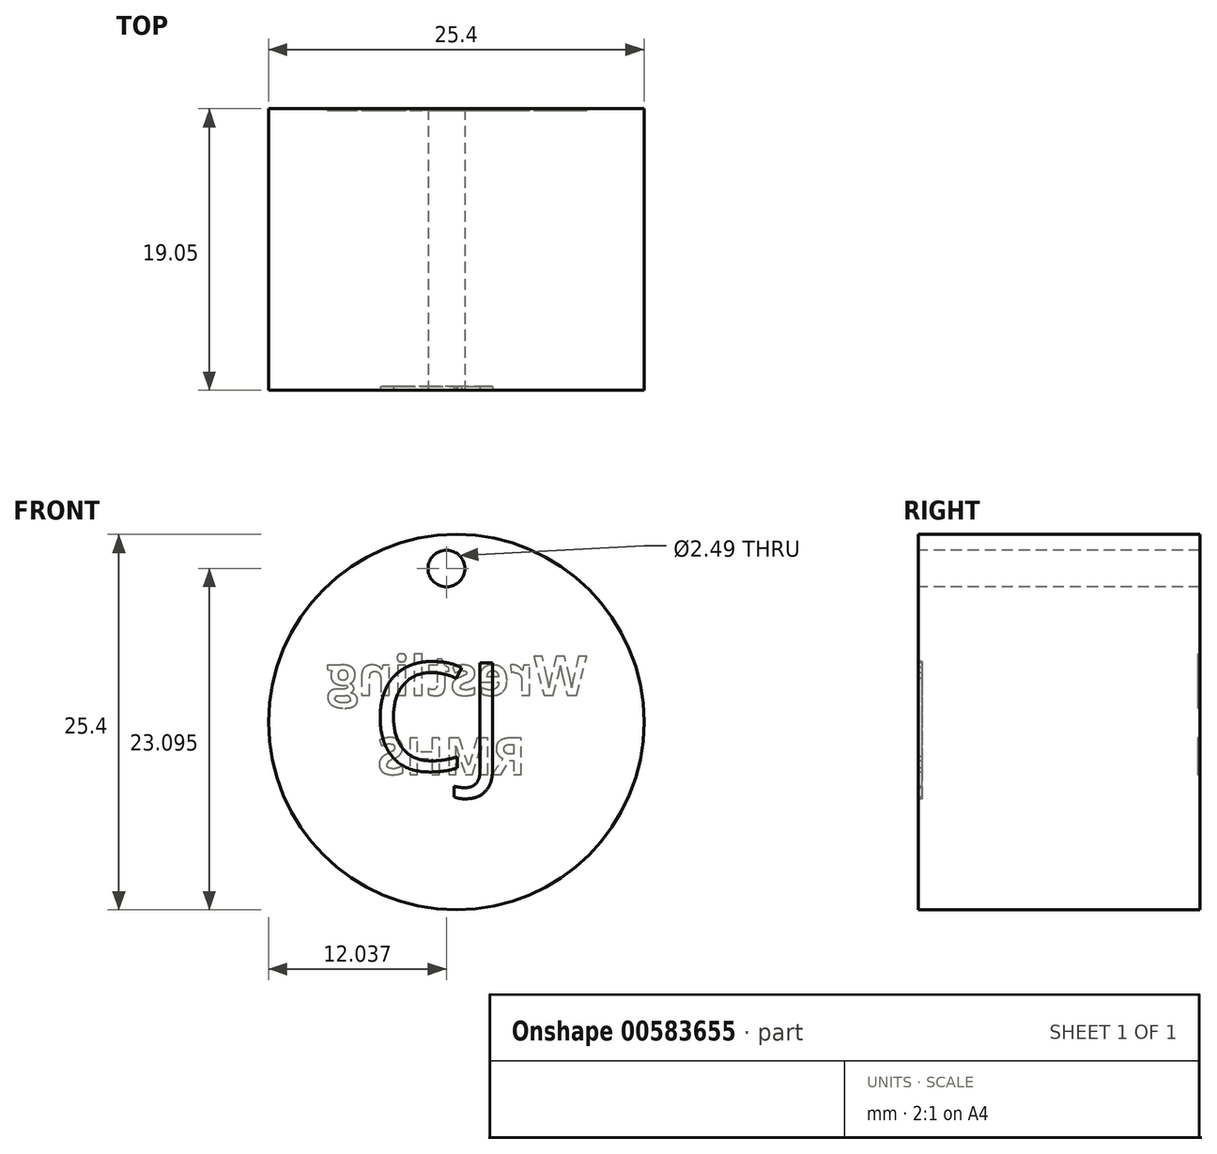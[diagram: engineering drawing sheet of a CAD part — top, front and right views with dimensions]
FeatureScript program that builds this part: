
annotation { "Feature Type Name" : "Feature", "Feature Type Description" : "" }
export const myFeature = defineFeature(function(context is Context, id is Id, definition is map)
    precondition{}
    {
        {
            var Q0;
            Q0=qCreatedBy(makeId("Front.planeOp"),FACE);
            var sketch = newSketch(context, id + "F0", { "sketchPlane" : qUnion([Q0])});
            skCircle(sketch, "E0", {"center": v(0.66, 0) * mm, "radius": 12.7 * mm});
            skSolve(sketch);
        }
        {
            var Q0;
            Q0 = qSketchRegion(id + "F0", true);
            extrude(context, id + "F1", {"entities" : qUnion([Q0]), "depth" : 19.05 * mm, "offsetDistance" : 25.4 * mm});
        }
        {
            var Q0;
            Q0=makeQuery(id+"F1.opExtrude","CAP_FACE",FACE,{"disambiguationData":[OSD([sQuery(id+"F0.wireOp",EDGE,"E0")])],"isStart":false});
            var sketch = newSketch(context, id + "F2", { "sketchPlane" : qUnion([Q0])});
            skText(sketch, "E1", { "text": "CJ", "fontName": "OpenSans-Regular.ttf"});
            const initialGuessF2  = {"E1": [-0.00511, -0.00327, 1, 0, 0.00734]};
            skSetInitialGuess(sketch, initialGuessF2);
            skSolve(sketch);
        }
        {
            var Q0;
            Q0 = qSketchRegion(id + "F2", true);
            extrude(context, id + "F3", {"entities" : qUnion([Q0]), "operationType" : NewBodyOperationType.REMOVE, "oppositeDirection" : true, "depth" : 0.25 * mm, "offsetDistance" : 25.4 * mm});
        }
        {
            var Q0;
            Q0=makeQuery(id+"F1.opExtrude","CAP_FACE",FACE,{"disambiguationData":[OSD([sQuery(id+"F0.wireOp",EDGE,"E0")])],"isStart":false});
            var sketch = newSketch(context, id + "F4", { "sketchPlane" : qUnion([Q0])});
            skCircle(sketch, "E2", {"center": v(0, 10.4) * mm, "radius": 1.24 * mm});
            skPoint(sketch, "E2.first.point", {"position": v(0, 11.64) * mm});
            skPoint(sketch, "E2.second.point", {"position": v(-1.06, 9.74) * mm});
            skPoint(sketch, "E2.third.point", {"position": v(0.96, 9.61) * mm});
            skSolve(sketch);
        }
        {
            var Q0;
            Q0 = qSketchRegion(id + "F4", true);
            extrude(context, id + "F5", {"entities" : qUnion([Q0]), "operationType" : NewBodyOperationType.REMOVE, "endBound" : BoundingType.THROUGH_ALL, "oppositeDirection" : true, "depth" : 25.4 * mm, "offsetDistance" : 25.4 * mm});
        }
        {
            var Q0;
            Q0=makeQuery(id+"F1.opExtrude","CAP_FACE",FACE,{"disambiguationData":[OSD([sQuery(id+"F0.wireOp",EDGE,"E0")])],"isStart":true});
            var sketch = newSketch(context, id + "F6", { "sketchPlane" : qUnion([Q0])});
            skText(sketch, "E3", { "text": "Wrestling", "fontName": "OpenSans-Bold.ttf"});
            const initialGuessF6  = {"E3": [-0.00948, 0.00183, 1, 0, 0.00265]};
            skSetInitialGuess(sketch, initialGuessF6);
            skSolve(sketch);
        }
        {
            var Q0;
            Q0 = qSketchRegion(id + "F6", true);
            extrude(context, id + "F7", {"entities" : qUnion([Q0]), "operationType" : NewBodyOperationType.REMOVE, "endBound" : BoundingType.SYMMETRIC, "depth" : 0.25 * mm, "offsetDistance" : 25.4 * mm});
        }
        {
            var Q0;
            {var subQ0=sQuery(id+"F0.wireOp",EDGE,"E0");Q0=makeQuery(id+"F7.boolean.opBoolean","SPLIT",FACE,{"disambiguationData":[TD([makeQuery(id+"F1.opExtrude","SWEPT_FACE",FACE,{"disambiguationData":[OSD([subQ0])]})])],"derivedFrom":makeQuery(id+"F1.opExtrude","CAP_FACE",FACE,{"disambiguationData":[OSD([subQ0])],"isStart":true})});}
            var sketch = newSketch(context, id + "F8", { "sketchPlane" : qUnion([Q0])});
            skText(sketch, "E4", { "text": "RMHS", "fontName": "OpenSans-Bold.ttf"});
            const initialGuessF8  = {"E4": [-0.00537, -0.00353, 1, 0, 0.00248]};
            skSetInitialGuess(sketch, initialGuessF8);
            skSolve(sketch);
        }
        {
            var Q0;
            Q0 = qSketchRegion(id + "F8", true);
            extrude(context, id + "F9", {"entities" : qUnion([Q0]), "operationType" : NewBodyOperationType.REMOVE, "endBound" : BoundingType.SYMMETRIC, "depth" : 0.25 * mm, "offsetDistance" : 25.4 * mm});
        }
    });
